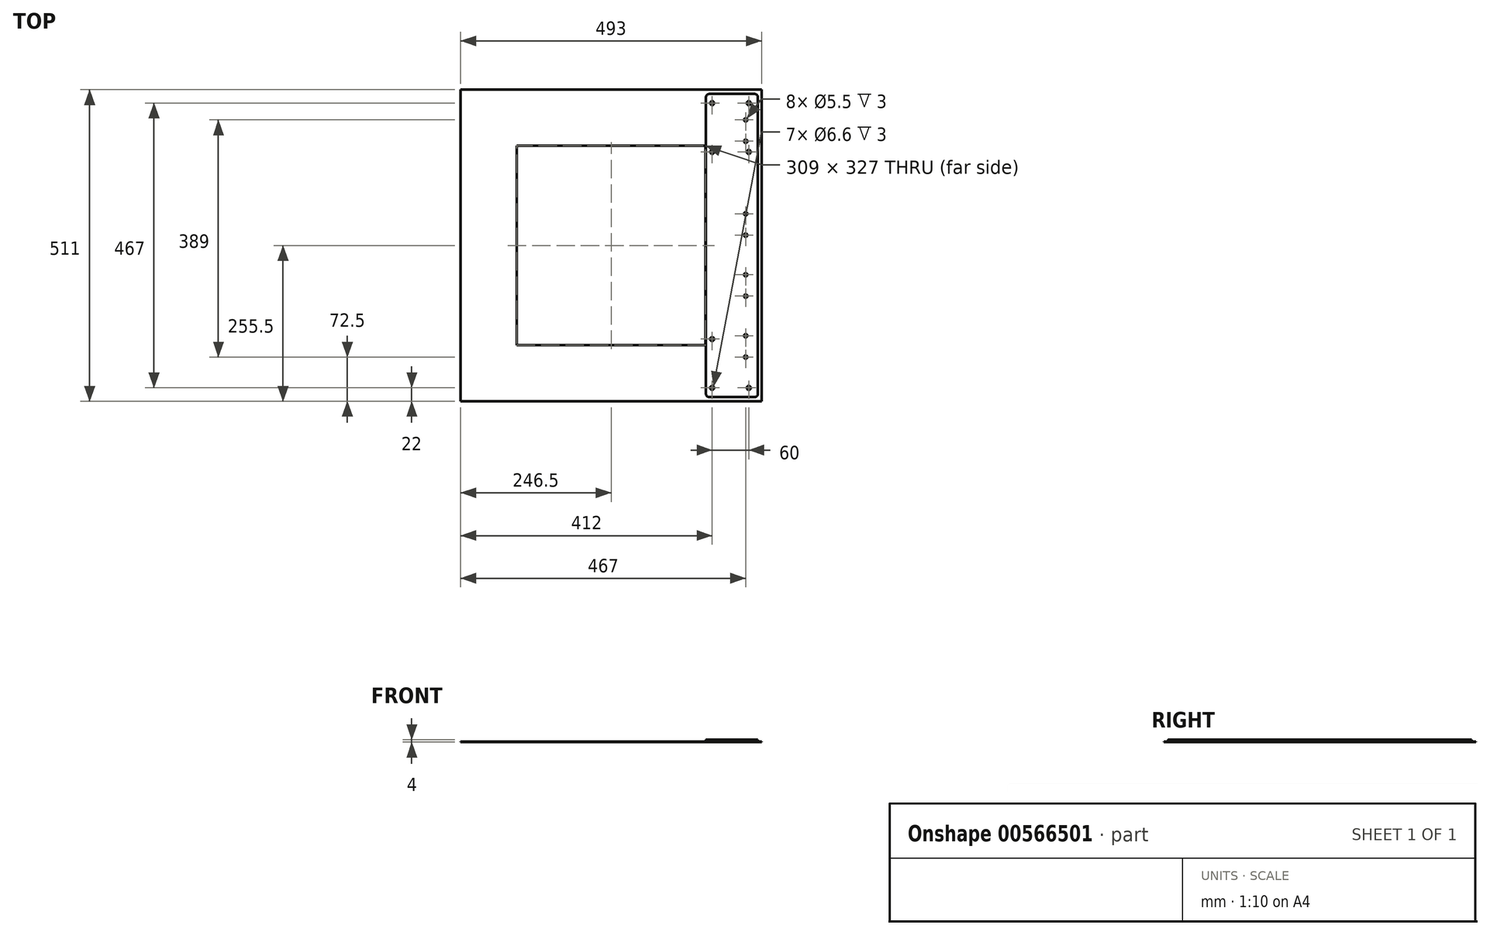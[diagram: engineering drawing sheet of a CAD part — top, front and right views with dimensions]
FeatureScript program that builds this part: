
annotation { "Feature Type Name" : "Feature", "Feature Type Description" : "" }
export const myFeature = defineFeature(function(context is Context, id is Id, definition is map)
    precondition{}
    {
        {
            var Q0;
            Q0=qCreatedBy(makeId("Top.planeOp"),FACE);
            var sketch = newSketch(context, id + "F0", { "sketchPlane" : qUnion([Q0])});
            skLineSegment(sketch, "E0.bottom", {"start": v(0, 0) * mm, "end": v(309, 0) * mm});
            skLineSegment(sketch, "E0.top", {"start": v(0, 327) * mm, "end": v(309, 327) * mm});
            skLineSegment(sketch, "E0.left", {"start": v(0, 0) * mm, "end": v(0, 327) * mm});
            skLineSegment(sketch, "E0.right", {"start": v(309, 0) * mm, "end": v(309, 327) * mm});
            skLineSegment(sketch, "E1.bottom", {"start": v(-92, -92) * mm, "end": v(401, -92) * mm});
            skLineSegment(sketch, "E1.top", {"start": v(-92, 419) * mm, "end": v(401, 419) * mm});
            skLineSegment(sketch, "E1.left", {"start": v(-92, -92) * mm, "end": v(-92, 419) * mm});
            skLineSegment(sketch, "E1.right", {"start": v(401, -92) * mm, "end": v(401, 419) * mm});
            skSolve(sketch);
        }
        {
            var Q0;
            Q0=makeQuery(id+"F0.imprint","IMPRINT",FACE,{"disambiguationData":[TD([[makeQuery(id+"F0.imprint","IMPRINT",EDGE,{"derivedFrom":sQuery(id+"F0.wireOp",EDGE,"E0.bottom")}),-1.0]])]});
            extrude(context, id + "F1", {"entities" : qUnion([Q0]), "depth" : 1 * mm, "offsetDistance" : 25 * mm});
        }
        {
            var Q0;
            Q0=makeQuery(id+"F1.opExtrude","CAP_FACE",FACE,{"disambiguationData":[OSD([sQuery(id+"F0.wireOp",EDGE,"E0.bottom"),sQuery(id+"F0.wireOp",EDGE,"E0.top"),sQuery(id+"F0.wireOp",EDGE,"E0.left"),sQuery(id+"F0.wireOp",EDGE,"E0.right"),sQuery(id+"F0.wireOp",EDGE,"E1.bottom"),sQuery(id+"F0.wireOp",EDGE,"E1.top"),sQuery(id+"F0.wireOp",EDGE,"E1.left"),sQuery(id+"F0.wireOp",EDGE,"E1.right")])],"isStart":false});
            var sketch = newSketch(context, id + "F2", { "sketchPlane" : qUnion([Q0])});
            skCircle(sketch, "E2", {"center": v(320, 10) * mm, "radius": 3.3 * mm});
            skLineSegment(sketch, "E3", {"start": v(320, 10) * mm, "end": v(393.83, 10) * mm, "construction": true});
            skLineSegment(sketch, "E4", {"start": v(380, 10) * mm, "end": v(380, -80.85) * mm, "construction": true});
            skCircle(sketch, "E5", {"center": v(380, 10) * mm, "radius": 3.3 * mm, "construction": true});
            skLineSegment(sketch, "E6", {"start": v(380, -70) * mm, "end": v(320, -70) * mm, "construction": true});
            skCircle(sketch, "E7", {"center": v(380, -70) * mm, "radius": 3.3 * mm});
            skCircle(sketch, "E8", {"center": v(320, -70) * mm, "radius": 3.3 * mm});
            skLineSegment(sketch, "E9", {"start": v(309, 163.5) * mm, "end": v(401, 163.5) * mm, "construction": true});
            skLineSegment(sketch, "E10", {"start": v(154.5, 327) * mm, "end": v(154.5, 419) * mm, "construction": true});
            skCircle(sketch, "E11.MirrorC", {"center": v(380, 397) * mm, "radius": 3.3 * mm});
            skCircle(sketch, "E12.MirrorC", {"center": v(380, 317) * mm, "radius": 3.3 * mm});
            skCircle(sketch, "E13.MirrorC", {"center": v(320, 317) * mm, "radius": 3.3 * mm});
            skCircle(sketch, "E14.MirrorC", {"center": v(320, 397) * mm, "radius": 3.3 * mm});
            skLineSegment(sketch, "E15.bottom", {"start": v(315, 412) * mm, "end": v(390, 412) * mm});
            skLineSegment(sketch, "E15.top", {"start": v(315, -85) * mm, "end": v(390, -85) * mm});
            skLineSegment(sketch, "E15.left", {"start": v(310, 407) * mm, "end": v(310, -80) * mm});
            skLineSegment(sketch, "E15.right", {"start": v(395, 407) * mm, "end": v(395, -80) * mm});
            skLineSegment(sketch, "E16.bottom", {"start": v(315, -100.6) * mm, "end": v(395, -100.6) * mm, "construction": true});
            skLineSegment(sketch, "E16.top", {"start": v(315, 429.43) * mm, "end": v(395, 429.43) * mm, "construction": true});
            skLineSegment(sketch, "E16.left", {"start": v(315, -100.6) * mm, "end": v(315, 429.43) * mm, "construction": true});
            skLineSegment(sketch, "E16.right", {"start": v(395, -100.6) * mm, "end": v(395, 429.43) * mm, "construction": true});
            skLineSegment(sketch, "E17", {"start": v(335, 429.43) * mm, "end": v(335, -100.6) * mm, "construction": true});
            skLineSegment(sketch, "E18", {"start": v(375, 429.43) * mm, "end": v(375, -100.6) * mm, "construction": true});
            skLineSegment(sketch, "E19.bottom", {"start": v(362.5, -42) * mm, "end": v(387.5, -42) * mm, "construction": true});
            skLineSegment(sketch, "E19.top", {"start": v(362.5, 38) * mm, "end": v(387.5, 38) * mm, "construction": true});
            skLineSegment(sketch, "E19.left", {"start": v(362.5, -42) * mm, "end": v(362.5, 38) * mm, "construction": true});
            skLineSegment(sketch, "E19.right", {"start": v(387.5, -42) * mm, "end": v(387.5, 38) * mm, "construction": true});
            skCircle(sketch, "E20", {"center": v(375, -19.5) * mm, "radius": 2.75 * mm});
            skCircle(sketch, "E21", {"center": v(375, 15.5) * mm, "radius": 2.75 * mm});
            skLineSegment(sketch, "E22", {"start": v(362.5, -2) * mm, "end": v(387.5, -2) * mm, "construction": true});
            skLineSegment(sketch, "E23", {"start": v(320, 397) * mm, "end": v(380, 397) * mm, "construction": true});
            skLineSegment(sketch, "E24.bottom", {"start": v(362.5, 392) * mm, "end": v(387.5, 392) * mm, "construction": true});
            skLineSegment(sketch, "E24.top", {"start": v(362.5, 312) * mm, "end": v(387.5, 312) * mm, "construction": true});
            skLineSegment(sketch, "E24.left", {"start": v(362.5, 392) * mm, "end": v(362.5, 312) * mm, "construction": true});
            skLineSegment(sketch, "E24.right", {"start": v(387.5, 392) * mm, "end": v(387.5, 312) * mm, "construction": true});
            skCircle(sketch, "E25", {"center": v(375, 369.5) * mm, "radius": 2.75 * mm});
            skCircle(sketch, "E26", {"center": v(375, 334.5) * mm, "radius": 2.75 * mm});
            skLineSegment(sketch, "E27", {"start": v(362.5, 352) * mm, "end": v(387.5, 352) * mm, "construction": true});
            skLineSegment(sketch, "E28", {"start": v(362.5, 48) * mm, "end": v(387.5, 48) * mm, "construction": true});
            skCircle(sketch, "E29.MirrorC", {"center": v(375, 80.5) * mm, "radius": 2.75 * mm});
            skCircle(sketch, "E30.MirrorC", {"center": v(375, 115.5) * mm, "radius": 2.75 * mm});
            skLineSegment(sketch, "E31", {"start": v(361.16, 148) * mm, "end": v(386.75, 148) * mm, "construction": true});
            skCircle(sketch, "E32.MirrorC", {"center": v(375, 180.5) * mm, "radius": 2.75 * mm});
            skCircle(sketch, "E33.MirrorC", {"center": v(375, 215.5) * mm, "radius": 2.75 * mm});
            skPoint(sketch, "E34.visualSharp", {"position": v(310, 412) * mm});
            skArc(sketch, "E34.filletArc", {"start": v(315, 412) * mm, "mid": v(311.46, 410.54) * mm, "end": v(310, 407) * mm});
            skPoint(sketch, "E35.visualSharp", {"position": v(395, 412) * mm});
            skArc(sketch, "E35.filletArc", {"start": v(395, 407) * mm, "mid": v(393.54, 410.54) * mm, "end": v(390, 412) * mm});
            skPoint(sketch, "E36.visualSharp", {"position": v(310, -85) * mm});
            skArc(sketch, "E36.filletArc", {"start": v(310, -80) * mm, "mid": v(311.46, -83.54) * mm, "end": v(315, -85) * mm});
            skPoint(sketch, "E37.visualSharp", {"position": v(395, -85) * mm});
            skArc(sketch, "E37.filletArc", {"start": v(390, -85) * mm, "mid": v(393.54, -83.54) * mm, "end": v(395, -80) * mm});
            skSolve(sketch);
        }
        {
            var Q0;
            Q0=makeQuery(id+"F2.imprint","IMPRINT",FACE,{"disambiguationData":[TD([[makeQuery(id+"F2.imprint","IMPRINT",EDGE,{"derivedFrom":sQuery(id+"F2.wireOp",EDGE,"E2")}),-1.0]])]});
            extrude(context, id + "F3", {"entities" : qUnion([Q0]), "operationType" : NewBodyOperationType.ADD, "depth" : 3 * mm, "offsetDistance" : 25 * mm});
        }
    });
